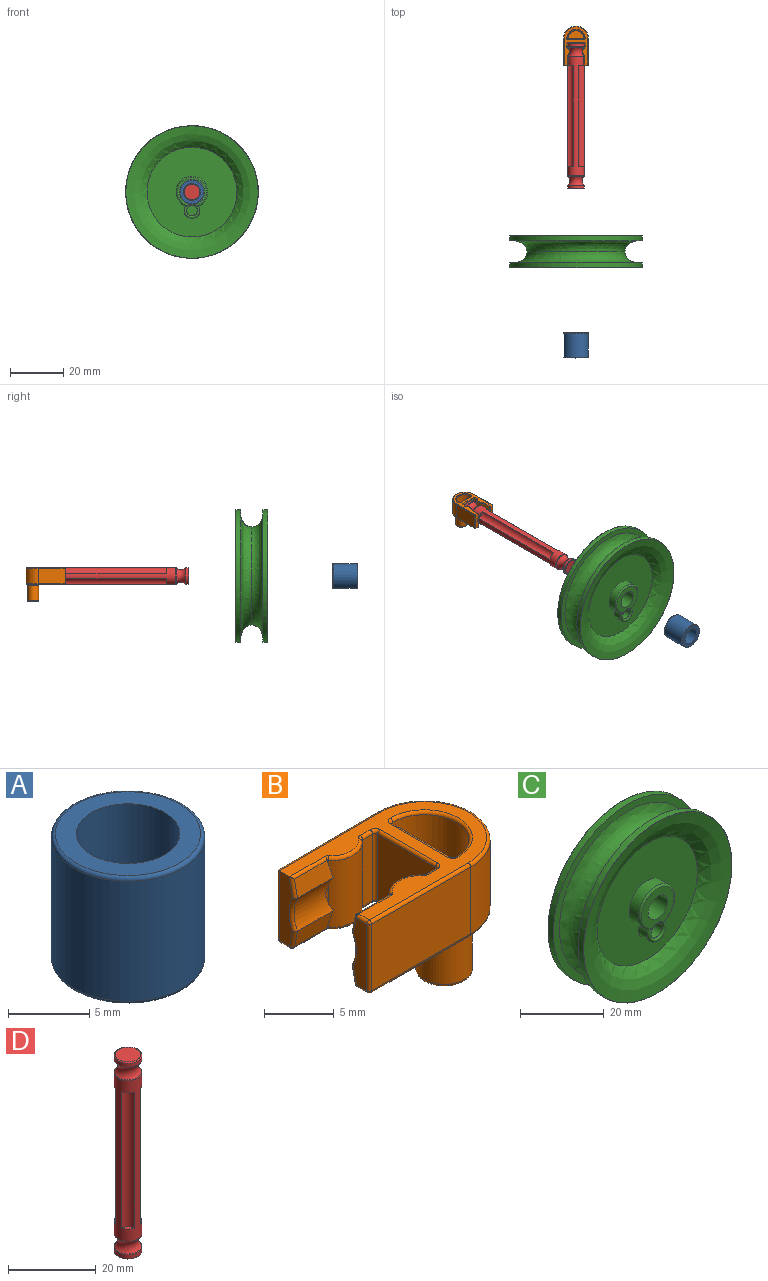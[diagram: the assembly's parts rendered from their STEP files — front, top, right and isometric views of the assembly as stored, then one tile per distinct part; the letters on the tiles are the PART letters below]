
ASSEMBLY  parts=4 mates=1
PART A: 6 faces, bbox 10.2x10.2x9.5 mm
  f0: torus R=4.46mm, axis (0,0,-1), area 11.6mm2, adj f1,f2
  f1: cylinder r=4.71mm len=9.42mm, axis (0,0,1), area 266.9mm2, adj f0,f3
  f2: plane 8.92x8.92mm, normal (0,0,-1), area 30.8mm2, adj f0,f5
  f3: torus R=4.46mm, axis (0,0,1), area 11.6mm2, adj f1,f4
  f4: plane 8.92x8.92mm, normal (0,0,1), area 30.8mm2, adj f3,f5
  f5: cylinder r=3.17mm len=9.53mm, axis (0,0,1), area 190mm2, adj f2,f4
PART B: 94 faces, bbox 15.4x10.2x12.8 mm
  f0: torus R=1.78mm, axis (0,0,-1), area 4.9mm2, adj f1,f2
  f1: cylinder r=2.03mm len=5.84mm, axis (0,0,-1), area 74.5mm2, adj f0,f3
  f2: plane 3.55x3.55mm, normal (0,0,-1), area 9.9mm2, adj f0
  f3: torus R=2.28mm, axis (0,0,1), area 5.3mm2, adj f1,f4
  f4: plane 14.48x8.89mm, normal (0,0,-1), area 50.3mm2, adj f3,f10,f12,f13,f14,f15,f37,f38
  f5: sphere r=0.25mm, area 0.1mm2, adj f10,f38,f39
  f6: sphere r=0.25mm, area 0.1mm2, adj f7,f12,f37
  f7: cylinder r=0.25mm len=1.57mm, axis (0,0.2,0.98), area 0.6mm2, adj f6,f8,f70,f85
  f8: torus R=3.43mm, axis (-1,0,0), area 1.2mm2, adj f7,f25,f70,f84
  f9: sphere r=0.25mm, area 0.1mm2, adj f10,f13,f23
  f10: cylinder r=0.25mm len=1.06mm, axis (0,-1,0), area 0.4mm2, adj f4,f5,f9,f92
  f11: sphere r=0.25mm, area 0.1mm2, adj f12,f15,f22
  f12: cylinder r=0.25mm len=1.06mm, axis (0,1,0), area 0.4mm2, adj f4,f6,f11,f70
  f13: cylinder r=0.25mm len=10.03mm, axis (1,0,0), area 4mm2, adj f4,f9,f14,f55
  f14: torus R=4.45mm, axis (0,0,-1), area 5.8mm2, adj f4,f13,f15,f93
  f15: cylinder r=0.25mm len=10.03mm, axis (-1,0,0), area 4mm2, adj f4,f11,f14,f90
  f16: sphere r=0.25mm, area 0.1mm2, adj f21,f24,f25
  f17: sphere r=0.25mm, area 0.1mm2, adj f18,f21,f22
  f18: cylinder r=0.25mm len=10.03mm, axis (1,0,0), area 4mm2, adj f17,f19,f54,f90
  f19: torus R=4.45mm, axis (0,0,1), area 5.8mm2, adj f18,f20,f54,f93
  f20: cylinder r=0.25mm len=10.29mm, axis (-1,0,0), area 4.1mm2, adj f19,f23,f54,f55
  f21: cylinder r=0.25mm len=1.06mm, axis (0,-1,0), area 0.4mm2, adj f16,f17,f54,f70
  f22: cylinder r=0.25mm len=5.84mm, axis (0,0,1), area 2.3mm2, adj f11,f17,f70,f90
  f23: cylinder r=0.25mm len=6.1mm, axis (0,0,-1), area 2.4mm2, adj f9,f20,f55,f92
  f24: cylinder r=0.25mm len=3.37mm, axis (-1,0,0), area 1.2mm2, adj f16,f26,f54,f86
  f25: cylinder r=0.25mm len=1.57mm, axis (0,-0.2,0.98), area 0.6mm2, adj f8,f16,f70,f86
  f26: torus R=0.51mm, axis (0,0,1), area 0mm2, adj f24,f27,f54,f56,f86
  f27: torus R=1.97mm, axis (0,0,1), area 1.5mm2, adj f26,f28,f54,f57
  f28: torus R=0.51mm, axis (0,0,1), area 0.1mm2, adj f27,f29,f54,f58
  f29: cylinder r=0.25mm len=1mm, axis (-1,0,0), area 0.4mm2, adj f28,f30,f54,f59
  f30: torus R=0.51mm, axis (0,0,1), area 0.2mm2, adj f29,f31,f54,f60
  f31: cylinder r=0.25mm len=5.84mm, axis (0,-1,0), area 2.3mm2, adj f30,f32,f54,f61
  f32: torus R=0.51mm, axis (0,0,1), area 0.2mm2, adj f31,f33,f54,f63
  f33: cylinder r=0.25mm len=1mm, axis (1,0,0), area 0.4mm2, adj f32,f34,f54,f64
  f34: torus R=0.51mm, axis (0,0,1), area 0.1mm2, adj f33,f35,f54,f66
  f35: torus R=1.97mm, axis (0,0,1), area 1.5mm2, adj f34,f36,f54,f67
  f36: torus R=0.51mm, axis (0,0,1), area 0mm2, adj f35,f40,f54,f62,f65
  f37: cylinder r=0.25mm len=3.37mm, axis (1,0,0), area 1.2mm2, adj f4,f6,f51,f85
  f38: cylinder r=0.25mm len=3.37mm, axis (-1,0,0), area 1.2mm2, adj f4,f5,f41,f69
  f39: cylinder r=0.25mm len=1.57mm, axis (0,-0.2,0.98), area 0.6mm2, adj f5,f52,f69,f92
  f40: cylinder r=0.25mm len=3.62mm, axis (1,0,0), area 1.2mm2, adj f36,f53,f54,f65
  f41: torus R=0.51mm, axis (0,0,-1), area 0mm2, adj f4,f38,f42,f69,f88
  f42: torus R=1.97mm, axis (0,0,-1), area 1.5mm2, adj f4,f41,f43,f67
  f43: torus R=0.51mm, axis (0,0,-1), area 0.1mm2, adj f4,f42,f44,f66
  f44: cylinder r=0.25mm len=1mm, axis (-1,0,0), area 0.4mm2, adj f4,f43,f45,f64
  f45: torus R=0.51mm, axis (0,0,-1), area 0.2mm2, adj f4,f44,f46,f63
  f46: cylinder r=0.25mm len=5.84mm, axis (0,1,0), area 2.3mm2, adj f4,f45,f47,f61
  f47: torus R=0.51mm, axis (0,0,-1), area 0.2mm2, adj f4,f46,f48,f60
  f48: cylinder r=0.25mm len=1mm, axis (1,0,0), area 0.4mm2, adj f4,f47,f49,f59
  f49: torus R=0.51mm, axis (0,0,-1), area 0.1mm2, adj f4,f48,f50,f58
  f50: torus R=1.97mm, axis (0,0,-1), area 1.5mm2, adj f4,f49,f51,f57
  f51: torus R=0.51mm, axis (0,0,-1), area 0mm2, adj f4,f37,f50,f85,f89
  f52: torus R=3.43mm, axis (1,0,0), area 1.2mm2, adj f39,f53,f68,f92
  f53: cylinder r=0.25mm len=1.83mm, axis (0,0.2,0.98), area 0.7mm2, adj f40,f52,f54,f65,f92
  f54: plane 14.73x8.89mm, normal (0,0,1), area 44.9mm2, adj f18,f19,f20,f21,f24,f26,f27,f28
  f55: plane 10.03x5.84mm, normal (0,1,0), area 58.6mm2, adj f13,f20,f23,f93
  f56: cylinder r=0.25mm len=0.19mm, axis (0,0,-1), area 0mm2, adj f26,f57,f86
  f57: cylinder r=2.22mm len=5.84mm, axis (0,0,-1), area 22mm2, adj f27,f50,f56,f58,f84,f85,f86,f89
  f58: cylinder r=0.25mm len=5.84mm, axis (0,0,-1), area 1.3mm2, adj f28,f49,f57,f59
  f59: plane 5.84x1mm, normal (0,1,0), area 5.9mm2, adj f29,f48,f58,f60
  f60: cylinder r=0.25mm len=5.84mm, axis (0,0,-1), area 2.3mm2, adj f30,f47,f59,f61
  f61: plane 5.84x5.84mm, normal (-1,0,0), area 34.1mm2, adj f31,f46,f60,f63
  f62: cylinder r=0.25mm len=0.19mm, axis (0,0,-1), area 0mm2, adj f36,f65,f67
  f63: cylinder r=0.25mm len=5.84mm, axis (0,0,-1), area 2.3mm2, adj f32,f45,f61,f64
  f64: plane 5.84x1mm, normal (0,-1,0), area 5.9mm2, adj f33,f44,f63,f66
  f65: plane 3.66x1.57mm, normal (0,-0.98,0.2), area 5.4mm2, adj f36,f40,f53,f62,f67,f68
  f66: cylinder r=0.25mm len=5.84mm, axis (0,0,-1), area 1.3mm2, adj f34,f43,f64,f67
  f67: cylinder r=2.22mm len=5.84mm, axis (0,0,-1), area 22mm2, adj f35,f42,f62,f65,f66,f68,f69,f87
  f68: cylinder r=3.17mm len=3.61mm, axis (1,0,0), area 10.1mm2, adj f52,f65,f67,f69,f87
  f69: plane 3.66x1.57mm, normal (0,-0.98,-0.2), area 5.4mm2, adj f38,f39,f41,f67,f68,f88
  f70: plane 5.84x1.35mm, normal (-1,0,0), area 6.8mm2, adj f7,f8,f12,f21,f22,f25
  f71: sphere r=0.25mm, area 0.1mm2, adj f78,f79,f80
  f72: sphere r=0.25mm, area 0.1mm2, adj f77,f79,f80
  f73: torus R=0.51mm, axis (0,0,-1), area 0.2mm2, adj f54,f75,f76,f78
  f74: torus R=0.51mm, axis (0,0,-1), area 0.2mm2, adj f54,f75,f76,f77
  f75: torus R=3.43mm, axis (0,0,-1), area 4.1mm2, adj f54,f73,f74,f81
  f76: cylinder r=0.25mm len=5.84mm, axis (0,1,0), area 2.3mm2, adj f54,f73,f74,f82
  f77: cylinder r=0.25mm len=3.3mm, axis (0,0,-1), area 1.3mm2, adj f72,f74,f81,f82
  f78: cylinder r=0.25mm len=3.3mm, axis (0,0,-1), area 1.3mm2, adj f71,f73,f81,f82
  f79: cylinder r=0.25mm len=5.84mm, axis (0,1,0), area 2.3mm2, adj f71,f72,f82,f83
  f80: torus R=2.92mm, axis (0,0,-1), area 3.9mm2, adj f71,f72,f81,f83
  f81: cylinder r=3.17mm len=6.35mm, axis (0,0,-1), area 33.2mm2, adj f75,f77,f78,f80
  f82: plane 5.84x3.3mm, normal (1,0,0), area 19.3mm2, adj f76,f77,f78,f79
  f83: plane 5.84x2.96mm, normal (0,0,1), area 13.6mm2, adj f79,f80
  f84: cylinder r=3.17mm len=3.61mm, axis (1,0,0), area 10.1mm2, adj f8,f57,f85,f86,f91
  f85: plane 3.66x1.57mm, normal (0,0.98,-0.2), area 5.4mm2, adj f7,f37,f51,f57,f84,f89
  f86: plane 3.66x1.57mm, normal (0,0.98,0.2), area 5.4mm2, adj f24,f25,f26,f56,f57,f84
  f87: cylinder r=0.25mm len=1.51mm, axis (0,0,-1), area 0.2mm2, adj f67,f68
  f88: cylinder r=0.25mm len=0.19mm, axis (0,0,-1), area 0mm2, adj f41,f67,f69
  f89: cylinder r=0.25mm len=0.19mm, axis (0,0,-1), area 0mm2, adj f51,f57,f85
  f90: plane 10.03x5.84mm, normal (0,-1,0), area 58.6mm2, adj f15,f18,f22,f93
  f91: cylinder r=0.25mm len=1.51mm, axis (0,0,-1), area 0.2mm2, adj f57,f84
  f92: plane 6.1x1.35mm, normal (-1,0,0), area 7.1mm2, adj f10,f23,f39,f52,f53,f54
  f93: cylinder r=4.7mm len=9.4mm, axis (0,0,1), area 86.2mm2, adj f14,f19,f55,f90
PART C: 87 faces, bbox 50x12x50 mm
  f0: plane 12.26x11.72mm, normal (0,1,0), area 76.1mm2, adj f13,f14,f19,f33,f35,f65,f66,f67
  f1: plane 12.63x11.82mm, normal (0,1,0), area 76.1mm2, adj f13,f19,f23,f36,f58,f59,f60,f61
  f2: plane 12.63x11.82mm, normal (0,1,0), area 76.1mm2, adj f13,f19,f24,f26,f51,f52,f53,f54
  f3: plane 12.26x11.72mm, normal (0,1,0), area 76.1mm2, adj f13,f19,f27,f29,f44,f45,f46,f47
  f4: plane 11.89x11.17mm, normal (0,1,0), area 76.1mm2, adj f13,f19,f30,f32,f37,f38,f39,f40
  f5: plane 50x50mm, normal (0,-1,0), area 309.3mm2, adj f8,f11
  f6: plane 50x50mm, normal (0,1,0), area 309.3mm2, adj f7,f9
  f7: revolved ~45.89x45.89mm, area 856.1mm2, adj f6,f8
  f8: revolved ~45.89x45.89mm, area 856.1mm2, adj f5,f7
  f9: cylinder r=25mm len=50mm, axis (0,1,0), area 282.7mm2, adj f6,f10
  f10: plane 50x50mm, normal (0,-1,0), area 8.3mm2, adj f9,f16
  f11: cylinder r=25mm len=50mm, axis (0,1,0), area 282.7mm2, adj f5,f12
  f12: plane 50x50mm, normal (0,1,0), area 8.3mm2, adj f11,f13
  f13: revolved ~49.89x49.89mm, area 1996.8mm2, adj f0,f1,f2,f3,f4,f12,f14,f22
  f14: revolved ~0.7x0.58mm, area 0mm2, adj f0,f13,f35
  f15: plane 33.89x33.89mm, normal (0,-1,0), area 768mm2, adj f16,f18,f73
  f16: revolved ~49.89x49.89mm, area 1176.7mm2, adj f10,f15
  f17: plane 11x10.71mm, normal (0,-1,0), area 59.5mm2, adj f21,f75,f76
  f18: cylinder r=6mm len=12mm, axis (0,-1,0), area 100.5mm2, adj f15,f73,f76
  f19: cylinder r=6mm len=12mm, axis (0,-1,0), area 75.6mm2, adj f0,f1,f2,f3,f4,f22,f23,f24
  f20: plane 11x11mm, normal (0,1,0), area 61.9mm2, adj f21,f77
  f21: cylinder r=3.25mm len=12mm, axis (0,-1,0), area 245mm2, adj f17,f20
  f22: plane 13.06x10.86mm, normal (0,1,0), area 87.7mm2, adj f13,f19,f85,f86
  f23: extruded ~12.13x3mm, area 17.9mm2, adj f1,f13,f19,f86
  f24: extruded ~12.13x3mm, area 17.9mm2, adj f2,f13,f19,f85
  f25: plane 14.09x11.25mm, normal (0,1,0), area 87.7mm2, adj f13,f19,f83,f84
  f26: extruded ~10.61x6.6mm, area 17.9mm2, adj f2,f13,f19,f84
  f27: extruded ~12.46x1.5mm, area 17.9mm2, adj f3,f13,f19,f83
  f28: plane 14.53x13.55mm, normal (0,1,0), area 87.7mm2, adj f13,f19,f81,f82
  f29: extruded ~9.56x8.05mm, area 17.9mm2, adj f3,f13,f19,f82
  f30: extruded ~11.58x4.7mm, area 17.9mm2, adj f4,f13,f19,f81
  f31: plane 14.72x14.26mm, normal (0,1,0), area 89mm2, adj f13,f19,f33,f80
  f32: extruded ~11.58x4.7mm, area 17.9mm2, adj f4,f13,f19,f80
  f33: extruded ~9.65x8.14mm, area 19.2mm2, adj f0,f13,f19,f31
  f34: plane 14.08x11.24mm, normal (0,1,0), area 87.7mm2, adj f13,f19,f78,f79
  f35: extruded ~12.46x1.5mm, area 17.8mm2, adj f0,f13,f14,f19,f79
  f36: extruded ~10.61x6.6mm, area 17.9mm2, adj f1,f13,f19,f78
  f37: plane 1.59x0.92mm, normal (0.5,0,0.87), area 1.1mm2, adj f4,f38,f42,f43
  f38: plane 1.59x0.92mm, normal (-0.5,0,0.87), area 1.1mm2, adj f4,f37,f39,f43
  f39: plane 1.84x0.6mm, normal (-1,0,0), area 1.1mm2, adj f4,f38,f40,f43
  f40: plane 1.59x0.92mm, normal (-0.5,0,-0.87), area 1.1mm2, adj f4,f39,f41,f43
  f41: plane 1.59x0.92mm, normal (0.5,0,-0.87), area 1.1mm2, adj f4,f40,f42,f43
  f42: plane 1.84x0.6mm, normal (1,0,0), area 1.1mm2, adj f4,f37,f41,f43
  f43: plane 3.68x3.19mm, normal (0,1,0), area 8.8mm2, adj f37,f38,f39,f40,f41,f42
  f44: plane 1.75x0.6mm, normal (0.31,0,0.95), area 1.1mm2, adj f3,f45,f49,f50
  f45: plane 1.37x1.23mm, normal (-0.67,0,0.74), area 1.1mm2, adj f3,f44,f46,f50
  f46: plane 1.8x0.6mm, normal (-0.98,0,-0.21), area 1.1mm2, adj f3,f45,f47,f50
  f47: plane 1.75x0.6mm, normal (-0.31,0,-0.95), area 1.1mm2, adj f3,f46,f48,f50
  f48: plane 1.37x1.23mm, normal (0.67,0,-0.74), area 1.1mm2, adj f3,f47,f49,f50
  f49: plane 1.8x0.6mm, normal (0.98,0,0.21), area 1.1mm2, adj f3,f44,f48,f50
  f50: plane 3.6x3.5mm, normal (0,1,0), area 8.8mm2, adj f44,f45,f46,f47,f48,f49
  f51: plane 1.49x1.08mm, normal (-0.81,0,0.59), area 1.1mm2, adj f2,f52,f56,f57
  f52: plane 1.68x0.75mm, normal (-0.91,0,-0.41), area 1.1mm2, adj f2,f51,f53,f57
  f53: plane 1.83x0.6mm, normal (-0.1,0,-0.99), area 1.1mm2, adj f2,f52,f54,f57
  f54: plane 1.49x1.08mm, normal (0.81,0,-0.59), area 1.1mm2, adj f2,f53,f55,f57
  f55: plane 1.68x0.75mm, normal (0.91,0,0.41), area 1.1mm2, adj f2,f54,f56,f57
  f56: plane 1.83x0.6mm, normal (0.1,0,0.99), area 1.1mm2, adj f2,f51,f55,f57
  f57: plane 3.66x3.36mm, normal (0,1,0), area 8.8mm2, adj f51,f52,f53,f54,f55,f56
  f58: plane 1.49x1.08mm, normal (-0.81,0,-0.59), area 1.1mm2, adj f1,f59,f63,f64
  f59: plane 1.83x0.6mm, normal (0.1,0,-0.99), area 1.1mm2, adj f1,f58,f60,f64
  f60: plane 1.68x0.75mm, normal (0.91,0,-0.41), area 1.1mm2, adj f1,f59,f61,f64
  f61: plane 1.49x1.08mm, normal (0.81,0,0.59), area 1.1mm2, adj f1,f60,f62,f64
  f62: plane 1.83x0.6mm, normal (-0.1,0,0.99), area 1.1mm2, adj f1,f61,f63,f64
  f63: plane 1.68x0.75mm, normal (-0.91,0,0.41), area 1.1mm2, adj f1,f58,f62,f64
  f64: plane 3.66x3.36mm, normal (0,1,0), area 8.8mm2, adj f58,f59,f60,f61,f62,f63
  f65: plane 1.75x0.6mm, normal (0.31,0,-0.95), area 1.1mm2, adj f0,f66,f70,f71
  f66: plane 1.8x0.6mm, normal (0.98,0,-0.21), area 1.1mm2, adj f0,f65,f67,f71
  f67: plane 1.37x1.23mm, normal (0.67,0,0.74), area 1.1mm2, adj f0,f66,f68,f71
  f68: plane 1.75x0.6mm, normal (-0.31,0,0.95), area 1.1mm2, adj f0,f67,f69,f71
  f69: plane 1.8x0.6mm, normal (-0.98,0,0.21), area 1.1mm2, adj f0,f68,f70,f71
  f70: plane 1.37x1.23mm, normal (-0.67,0,-0.74), area 1.1mm2, adj f0,f65,f69,f71
  f71: plane 3.6x3.5mm, normal (0,1,0), area 8.8mm2, adj f65,f66,f67,f68,f69,f70
  f72: cylinder r=2mm len=4mm, axis (0,-1,0), area 44mm2, adj f74,f75
  f73: cylinder r=3mm len=6mm, axis (0,-1,0), area 39.5mm2, adj f15,f18,f75
  f74: plane 4x4mm, normal (0,-1,0), area 12.6mm2, adj f72
  f75: torus R=2.5mm, axis (0,-1,0), area 20.7mm2, adj f17,f72,f73,f76
  f76: torus R=5.5mm, axis (0,-1,0), area 25.2mm2, adj f17,f18,f75
  f77: torus R=5.5mm, axis (0,-1,0), area 28.7mm2, adj f19,f20
  f78: bspline ~11.59x7.06mm, area 2mm2, adj f13,f19,f34,f36
  f79: bspline ~13.42x1.55mm, area 2mm2, adj f13,f19,f34,f35
  f80: bspline ~12.32x5.22mm, area 2mm2, adj f13,f19,f31,f32
  f81: bspline ~14.74x6.96mm, area 2mm2, adj f13,f19,f28,f30
  f82: bspline ~10.2x8.79mm, area 2mm2, adj f13,f19,f28,f29
  f83: bspline ~13.35x1.62mm, area 2mm2, adj f13,f19,f25,f27
  f84: bspline ~11.59x7.06mm, area 2mm2, adj f13,f19,f25,f26
  f85: bspline ~13.22x3.15mm, area 2mm2, adj f13,f19,f22,f24
  f86: bspline ~13.22x3.15mm, area 2mm2, adj f13,f19,f22,f23
PART D: 25 faces, bbox 9.8x9.8x54.9 mm
  f0: torus R=2.92mm, axis (0,0,1), area 7.7mm2, adj f1,f2
  f1: cylinder r=3.17mm len=6.35mm, axis (0,0,-1), area 20mm2, adj f0,f3
  f2: plane 5.84x5.84mm, normal (0,0,-1), area 26.8mm2, adj f0
  f3: torus R=2.92mm, axis (0,0,1), area 4.4mm2, adj f1,f8
  f4: torus R=2.92mm, axis (0,0,1), area 4.4mm2, adj f8,f15
  f5: plane 2.05x2.05mm, normal (0,0,1), area 1.8mm2, adj f15,f19
  f6: plane 2.05x2.05mm, normal (0,0,1), area 1.8mm2, adj f15,f18
  f7: plane 2.05x2.05mm, normal (0,0,1), area 1.8mm2, adj f15,f16
  f8: torus R=4.51mm, axis (0,0,1), area 62.5mm2, adj f3,f4
  f9: plane 2.05x2.05mm, normal (0,0,1), area 1.8mm2, adj f15,f17
  f10: torus R=2.92mm, axis (0,0,-1), area 7.7mm2, adj f11,f12
  f11: cylinder r=3.17mm len=6.35mm, axis (0,0,-1), area 20mm2, adj f10,f13
  f12: plane 5.84x5.84mm, normal (0,0,1), area 26.8mm2, adj f10
  f13: torus R=2.92mm, axis (0,0,-1), area 4.4mm2, adj f11,f23
  f14: torus R=2.92mm, axis (0,0,-1), area 4.4mm2, adj f15,f23
  f15: cylinder r=3.17mm len=44.8mm, axis (0,0,-1), area 436.5mm2, adj f4,f5,f6,f7,f9,f14,f16,f17
  f16: cylinder r=2.22mm len=37.95mm, axis (0,0,-1), area 119.9mm2, adj f7,f15,f22
  f17: cylinder r=2.22mm len=37.95mm, axis (0,0,-1), area 119.9mm2, adj f9,f15,f24
  f18: cylinder r=2.22mm len=37.95mm, axis (0,0,-1), area 119.9mm2, adj f6,f15,f21
  f19: cylinder r=2.22mm len=37.95mm, axis (0,0,-1), area 119.9mm2, adj f5,f15,f20
  f20: plane 2.05x2.05mm, normal (0,0,-1), area 1.8mm2, adj f15,f19
  f21: plane 2.05x2.05mm, normal (0,0,-1), area 1.8mm2, adj f15,f18
  f22: plane 2.05x2.05mm, normal (0,0,-1), area 1.8mm2, adj f15,f16
  f23: torus R=4.51mm, axis (0,0,-1), area 62.5mm2, adj f13,f14
  f24: plane 2.05x2.05mm, normal (0,0,-1), area 1.8mm2, adj f15,f17
PLACE A rot(axis=(-1,0,0),90deg) t=(18.44,-43.35,23.91)mm
PLACE B rot(axis=(0,0,1),90deg) t=(18.44,77.1,20.73)mm
PLACE C t=(18.44,2.67,23.91)mm
PLACE D rot(axis=(1,0,0),90deg) t=(15.26,20.37,23.91)mm
MATE fastened B.f8 <-> D.f10  axis (0,-1,0) through (18.44,75.29,23.91)mm
